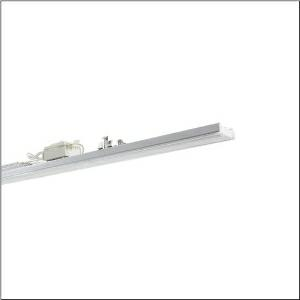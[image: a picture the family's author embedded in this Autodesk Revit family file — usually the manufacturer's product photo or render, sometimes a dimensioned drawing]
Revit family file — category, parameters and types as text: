
# Revit family: licross_11_recessed_extreme_mo_51te18dn485ge
name_source: partatom
category: Lighting Fixtures
units: mm (PartAtom-declared; Revit-internal decimal feet)

## family parameters
Cut with Voids When Loaded = No
Host = Face
Light Source = No
Part Type = Normal
Room Calculation Point = No
Round Connector Dimension = Use Diameter
Shared = No

## types (1)
- --- (1 x LED, 8910 lm, 50.3 W, 4000K)
    Apparent Load = 50 VA
    CIE Flux Codes = 83 96 99 100 100
    Color Rendering = 80
    Color Temperature = 4000K
    Default Elevation = 1800 mm
    Description = Licross 11 Recessed extreme MO, luminaire insert, of sheet steel, galvanised, coil coated, white, length: 1.500mm, width: 66mm, height: 67mm, LED rated luminous flux: 8.910lm, light colour: 840, SDCM (Standard Deviation of Colour Matching)MacAdam ≤ 2 SDCM (initial), control gear: DALI 2, with plug, 5-pole, with phase selection, mains connection: 220..240V, AC, 50/60Hz, rated input power: 50W, internal wiring halogen-free, primary light control with lens, of plastic, primary optical cover: cover, of PMMA, light emission: direct distribution, primary light characteristic: symmetric, protection rating (complete): IP54, insulation class (complete): insulation class I (protective earthing), certification: CE, ENEC, VDE, UKCA, protection symbol: D if used in an environment with non-conductive dust loads with corresponding accessories, impact resistance: IK06, permissible ambient temperature for indoor applications: -25..+45°C, corresponds to IFS (International Featured Standards) requirements for safety and quality in the food industry, reducing of maximum allowable ambient temperature of 5°C with ceiling mounting, LABS conformity tested according to VDMA 24364:2018-05, The light source and the operating device comply with the requirements of the Ecodesign Regulation (EU) 2019/2020 and are replaceable in accordance with this regulation, packaging unit: 1 piece
    Height = 58 mm
    Lamp = 1 x LED
    Lamp Light Flux = 8910 lm
    Lamp Power = 50.3 W
    Lamp count = 1
    Length = 1500 mm
    Luminous efficacy = 177 lm/W
    Manufacturer = Siteco
    ModVariant = No
    Model = 51TE18DN485GE
    Mounting Place = Ceiling
    Mounting Type = Pendant
    Number of Poles = 1
    OnlyDefault = Yes
    Power Factor = 1
    Product Name = Licross 11 Recessed extreme MO
    Product group = luminaire insert | ceiling pendant
    ProductGroupID = 901
    Protection Class = Protection class I
    Protection Degree = IP 54
    RLX_Detail_Level = 1
    RLX_Emergency_Light_Flux = 0 lm
    RLX_Emergency_Type = 0
    RLX_Emergency_Type_DB = No
    RlxData = <blob elided: 24905 chars, md5=ca8fb093>
    Socket = socket
    Standby Power = 0 W
    System Light Flux = 8910 lm
    System Power = 50 W
    Type Comments = factory setting: luminous flux: 100 % | dim-lin: 254 | 335 mA
    Type Image = l_1296930.jpg
    URL = http://relux.com
    VarID = @adj_093667
    Voltage = 0 V
    Weight = 0.00 kg
    Width = 66 mm

## geometry (parser evidence)
native form markers: Blend x4, Sweep x11
no freeform markers — native parametric forms only
